# Revit family: RRPOSTM-SPCBP
name_source: partatom
category: Generic Models
revit_build: Autodesk Revit 2018 (Build: 20190510_1515(x64)
units: mm (PartAtom-declared; Revit-internal decimal feet)

## family parameters
Always vertical = No
Can host rebar = No
Cut with Voids When Loaded = No
Part Type = Normal
Room Calculation Point = No
Round Connector Dimension = Use Diameter
Shared = Yes
Work Plane-Based = Yes

## types (3) — shared parameters
Cap Height = 1.5 "
Default Elevation = 48 "
Diameter = 2.38 "
Patent Information = 10495237, 10,697,562, 10,844,978, 11,262,000
Post Plate Height = 0.5 "

## per-type parameters (varying)
| type | Catalog Number | Description | Height | Post Height |
| RRPOSTM30448-SPCBP | RRPOSTM30436-SPCBP | One Roof Top Post Mount  2 Inch Schedule 40 Pipe 304 w/ 6 Inch X 12 Inch Base 304 48 Inch High | 48 " | 46 " |
| RRPOSTM30460-SPCBP | RRPOSTM30460-SPCBP | One Roof Top Post Mount  2 Inch Schedule 40 Pipe 304 w/ 6 Inch X 12 Inch Base 304 60 Inch High | 60 " | 58 " |
| RRPOSTM30436-SPCBP | RRPOSTM30436-SPCBP | One Roof Top Post Mount  2 Inch Schedule 40 Pipe 304 w/ 6 Inch X 12 Inch Base 304 36 Inch High | 36 " | 34 " |

## geometry (parser evidence)
native form markers: Sweep x9
no freeform markers — native parametric forms only
